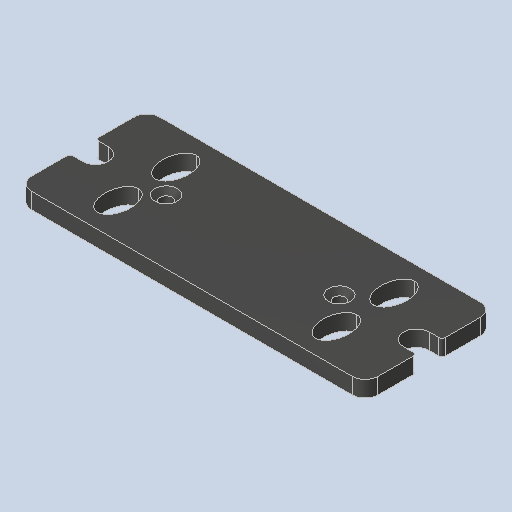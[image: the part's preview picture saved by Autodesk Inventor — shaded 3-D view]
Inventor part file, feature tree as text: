
AUTODESK INVENTOR PART (.ipt)
format: ipt  version: 2023.4 (Build 274418000, 418)  size: 123,904 bytes
history: native  units: in
note: dims shown in document units (in); Inventor stores cm internally (conversion verified against a paired STEP export)
features: mirror x1
ambient origin geometry x8: Origin, YZ Plane, XZ Plane, XY Plane, X Axis, Y Axis, Z Axis, Center Point
bodies: Solid1 (feature_tree)
feature tree (1):
  mirror  "Mirror2"
